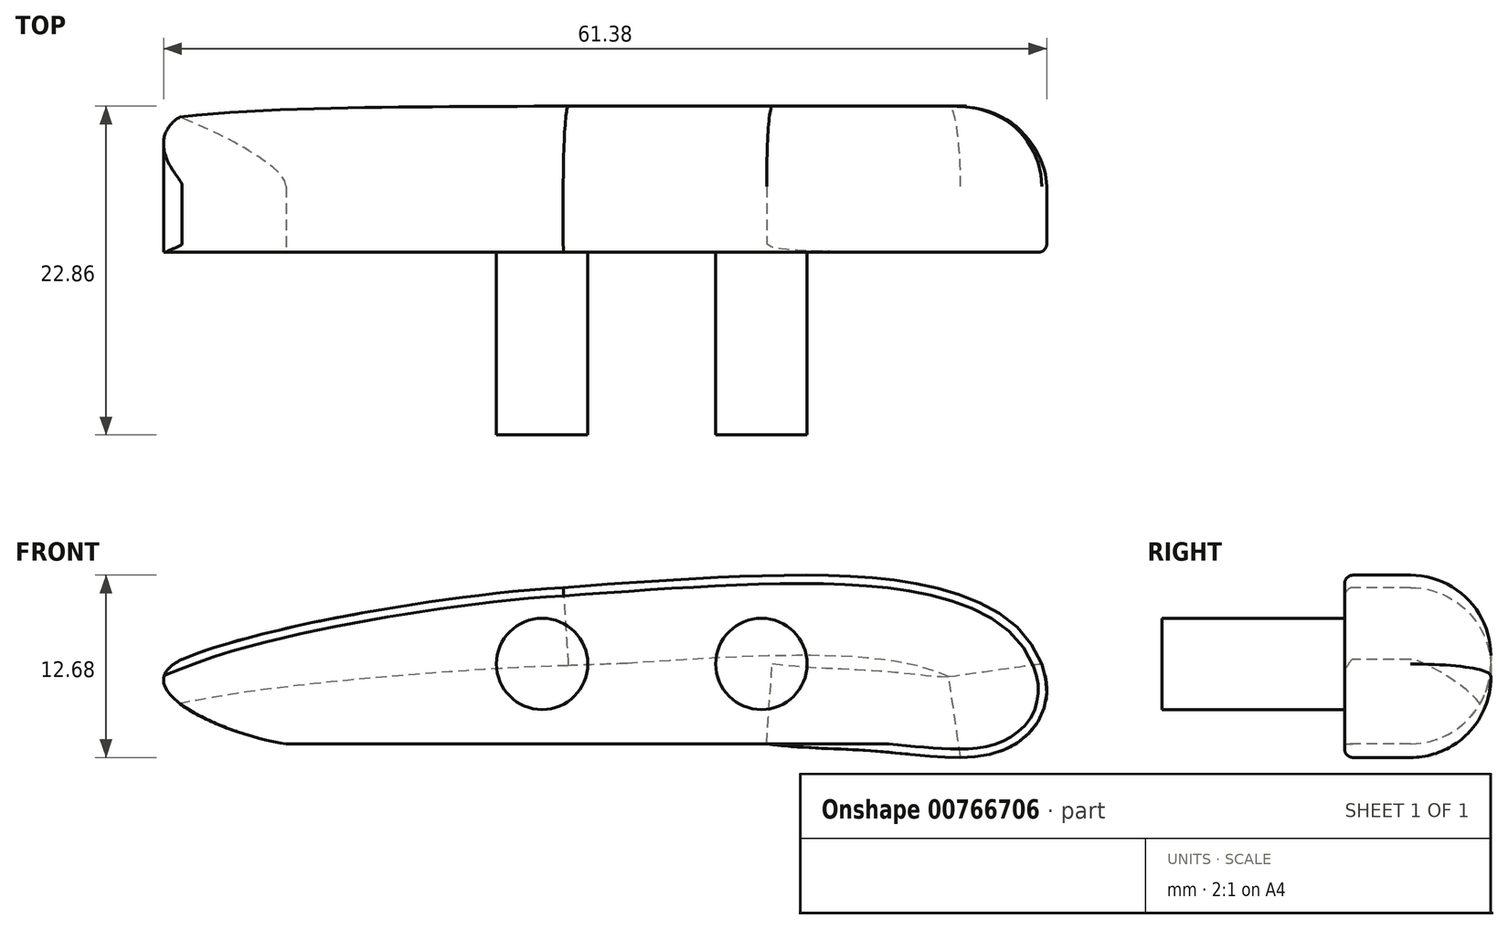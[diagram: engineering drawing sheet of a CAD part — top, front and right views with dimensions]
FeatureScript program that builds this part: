
annotation { "Feature Type Name" : "Feature", "Feature Type Description" : "" }
export const myFeature = defineFeature(function(context is Context, id is Id, definition is map)
    precondition{}
    {
        {
            var Q0;
            Q0=qCreatedBy(makeId("Front.planeOp"),FACE);
            var sketch = newSketch(context, id + "F0", { "sketchPlane" : qUnion([Q0])});
            skCircle(sketch, "E0", {"center": v(9.34, 19.4) * mm, "radius": 3.18 * mm});
            skCircle(sketch, "E1", {"center": v(-5.9, 19.4) * mm, "radius": 3.18 * mm});
            skLineSegment(sketch, "E2", {"start": v(-5.9, 13.84) * mm, "end": v(9.7, 13.84) * mm});
            skLineSegment(sketch, "E3", {"start": v(-5.9, 13.84) * mm, "end": v(-23.68, 13.84) * mm});
            skFitSpline(sketch, "E4", {"points": [v(-23.68, 13.84) * mm, v(-30.92, 19.72) * mm], "startDerivative": vector(-11.67, 1.56) * mm, "endDerivative": vector(13.07, 6.38) * mm});
            skFitSpline(sketch, "E5", {"points": [v(-30.92, 19.72) * mm, v(-4.43, 24.7) * mm], "startDerivative": vector(20.37, 8.2) * mm, "endDerivative": vector(17.93, 0.91) * mm});
            skFitSpline(sketch, "E6", {"points": [v(-4.43, 24.7) * mm, v(21.42, 24.7) * mm, v(27.75, 21.26) * mm, v(29.05, 16.56) * mm, v(25.83, 13.28) * mm, v(19.17, 13.16) * mm, v(14.52, 13.5) * mm, v(9.7, 13.84) * mm], "startDerivative": vector(150.1, 11.51) * mm, "endDerivative": vector(-44, 6.2) * mm});
            skLineSegment(sketch, "E7", {"start": v(9.34, 19.4) * mm, "end": v(33.23, 19.4) * mm});
            skSolve(sketch);
        }
        {
            var Q0;
            Q0=makeQuery(id+"F0.imprint","IMPRINT",FACE,{"disambiguationData":[TD([[makeQuery(id+"F0.imprint","IMPRINT",EDGE,{"derivedFrom":sQuery(id+"F0.wireOp",EDGE,"E0")}),-1.0]])]});
            var Q1;
            Q1=makeQuery(id+"F0.imprint","IMPRINT",FACE,{"disambiguationData":[TD([[makeQuery(id+"F0.imprint","IMPRINT",EDGE,{"derivedFrom":sQuery(id+"F0.wireOp",EDGE,"E1")}),1.0]])]});
            var Q2;
            Q2=makeQuery(id+"F0.imprint","IMPRINT",FACE,{"disambiguationData":[TD([[makeQuery(id+"F0.imprint","IMPRINT",EDGE,{"derivedFrom":sQuery(id+"F0.wireOp",EDGE,"E0")}),1.0]])]});
            extrude(context, id + "F1", {"entities" : qUnion([Q0, Q1, Q2]), "depth" : 10.16 * mm, "offsetDistance" : 25.4 * mm});
        }
        {
            var Q0;
            Q0=makeQuery(id+"F1.opExtrude","CAP_EDGE",EDGE,{"disambiguationData":[OSD([sQuery(id+"F0.wireOp",EDGE,"E6")])],"isStart":false});
            var Q1;
            Q1=makeQuery(id+"F1.opExtrude","CAP_EDGE",EDGE,{"disambiguationData":[OSD([sQuery(id+"F0.wireOp",EDGE,"E5")])],"isStart":false});
            var Q2;
            Q2=makeQuery(id+"F1.opExtrude","CAP_EDGE",EDGE,{"disambiguationData":[OSD([sQuery(id+"F0.wireOp",EDGE,"E2"),sQuery(id+"F0.wireOp",EDGE,"E3")])],"isStart":false});
            fillet(context, id + "F2", {"entities" : qUnion([Q0, Q1, Q2]), "radius" : 5.6 * mm, "tangentPropagation" : true, "allowEdgeOverflow" : false});
        }
        {
            var Q0;
            Q0=makeQuery(id+"F0.imprint","IMPRINT",FACE,{"disambiguationData":[TD([[makeQuery(id+"F0.imprint","IMPRINT",EDGE,{"derivedFrom":sQuery(id+"F0.wireOp",EDGE,"E0")}),1.0]])]});
            var Q1;
            Q1=makeQuery(id+"F0.imprint","IMPRINT",FACE,{"disambiguationData":[TD([[makeQuery(id+"F0.imprint","IMPRINT",EDGE,{"derivedFrom":sQuery(id+"F0.wireOp",EDGE,"E1")}),1.0]])]});
            extrude(context, id + "F3", {"entities" : qUnion([Q0, Q1]), "operationType" : NewBodyOperationType.ADD, "depth" : -12.7 * mm, "offsetDistance" : 25.4 * mm});
        }
        {
            var Q0;
            Q0=makeQuery(id+"F1.opExtrude","CAP_EDGE",EDGE,{"disambiguationData":[OSD([sQuery(id+"F0.wireOp",EDGE,"E6")])],"isStart":true});
            fillet(context, id + "F4", {"entities" : qUnion([Q0]), "radius" : 0.58 * mm, "tangentPropagation" : true, "allowEdgeOverflow" : false});
        }
        {
            var Q0;
            Q0=makeQuery(id+"F1.opExtrude","SWEPT_BODY",BODY,{"disambiguationData":[OSD([sQuery(id+"F0.wireOp",EDGE,"E2"),sQuery(id+"F0.wireOp",EDGE,"E3"),sQuery(id+"F0.wireOp",EDGE,"E4"),sQuery(id+"F0.wireOp",EDGE,"E5"),sQuery(id+"F0.wireOp",EDGE,"E6")])]});
            var Q1;
            Q1=qCreatedBy(makeId("Front.planeOp"),FACE);
            mirror(context, id + "F5", {"entities" : qUnion([Q0]), "mirrorPlane" : qUnion([Q1])});
        }
        {
            var Q0;
            Q0=makeQuery(id+"F1.opExtrude","SWEPT_BODY",BODY,{"disambiguationData":[OSD([sQuery(id+"F0.wireOp",EDGE,"E2"),sQuery(id+"F0.wireOp",EDGE,"E3"),sQuery(id+"F0.wireOp",EDGE,"E4"),sQuery(id+"F0.wireOp",EDGE,"E5"),sQuery(id+"F0.wireOp",EDGE,"E6")])]});
            deleteBodies(context, id + "F6", {"entities" : qUnion([Q0])});
        }
    });
